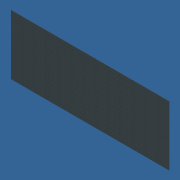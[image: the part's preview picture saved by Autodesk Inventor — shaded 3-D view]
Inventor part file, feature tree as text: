
AUTODESK INVENTOR PART (.ipt)
format: ipt  version: unknown  size: 160,256 bytes
history: native  units: in
note: dims shown in document units (in); Inventor stores cm internally (conversion verified against a paired STEP export)
features: extrude x1, sketch x1
ambient origin geometry x8: Origin, YZ Plane, XZ Plane, XY Plane, X Axis, Y Axis, Z Axis, Center Point
bodies: Solid1 (feature_tree)
feature tree (2):
  extrude  "Extrusion1"  Depth=34.5in
  sketch  "Sketch1"  dims[d0=91.0in d1=34.5in d2=0.125in d3=0.0in]
